# Revit family: Deca_Sifão para cozinha_1682.112
name_source: partatom
category: Plumbing Fixtures
units: mm (PartAtom-declared; Revit-internal decimal feet)

## family parameters
Cut with Voids When Loaded = No
Host = Face
Part Type = Normal
Room Calculation Point = No
Round Connector Dimension = Use Radius
Shared = No

## types (1)
- 1682.C.100.112_Cromado
    Acompanha o Produto = -
    Aprovado por = quattroD
    Atendimento ao Cliente = 0800-0117073
    CWFU = 0
    Categoria = COMPLEMENTARES
    Composição Anel Vedação = -
    Composição Assento = -
    Composição Básica = Liga de Cobre (bronze e latão),Plásticos de Engenharia,Elastômeros
    Composição Componente = -
    Consumo = -
    Cor Interna = -
    Cor Principal = Cromado
    Cor Secundária = -
    Cores Componente = -
    Criado por = quattroD
    Código Pai = 1682.100.112
    Default Elevation = 0 mm  [stored 0 ft]
    Description = Sifão articulado para lavatório
    Diâmetro Entrada de Esgoto = 40 mm  [stored 0.131234 ft]
    Diâmetro Ponto de Esgoto = 40 mm  [stored 0.131234 ft]
    Informações Complementares = -
    Itens de Instalação = -
    Linha = Sifões Competitivo
    Manufacturer = Deca
    Material = Deca_Cromado
    Model = 1682.C.100.112
    Norma = NBR14162
    Peso Líquido (Kg) = 1.416
    Pressão máx. funcionamento = -
    Pressão mín. Aquec. Acúmulo = -
    Pressão mín. Aquec. Passagem = -
    Pressão mín. funcionamento = -
    Raio Entrada de Esgoto = 20 mm  [stored 0.0656168 ft]
    Raio Ponto de Esgoto = 20 mm  [stored 0.0656168 ft]
    Saída de Esgoto = -
    Segmento = Banheiro Competitivo
    Tipo de dispositivo economizador = -
    Tipo de mecanismo utilizado = -
    Tipo de rosca de entrada = BSP NBR 8133
    Tipo de rosca de saída = -
    URL = www.deca.com.br
    Vazão na Pressão máx. (L/min) = -
    Vazão na Pressão mín. (L/min) = -
    WFU = 0

note: [stored X ft] marks values corroborated as IEEE doubles in the binary element streams (Revit-internal decimal feet)

## geometry (parser evidence)
native form markers: Sweep x13
no freeform markers — native parametric forms only
